# Revit family: Hydrablock P 22 30 T
name_source: partatom
category: Attrezzatura meccanica
units: mm (PartAtom-declared; Revit-internal decimal feet)

## family parameters
Basato su piano di lavoro = No
Condiviso = No
Mantieni orientamento annotazione = No
Numero OmniClass = 23.75.00.00
Punto di calcolo locali = No
Quota connettore circolare = Usa diametro
Sempre verticale = Sì
Taglio con vuoti quando caricato = No
Tipo di parte = Normale
Titolo OmniClass = Climate Control (HVAC)

## types (2) — shared parameters
Casing color = SB2014
Compressor = 1
Condensation = air
Depth = 440 mm  [stored 1.44357 ft]
Descrizione = High efficiency air cooled
Drain piping = 25 mm  [stored 0.082021 ft]
Gas = R32
Height = 1558 mm  [stored 5.11155 ft]
Installation = Outdoor installation
Min cable selection (power wiring) = 4×6 mm2 + 1×6 mm2
Power supply = 380-415V 3N~50Hz
Produttore = Midea
Series = M thermal
Water piping connections = 32 mm  [stored 0.104987 ft]
Width = 1129 mm  [stored 3.70407 ft]
clearance access behind = 300 mm
clearance access front = 3000 mm  [stored 9.84252 ft]
clearance access left = 300 mm
clearance access right = 600 mm  [stored 1.9685 ft]
zero-valued in all types: Prospetto di default

## per-type parameters (varying)
| type | Air Flow | Cooling Power Input (EWT 23⁰C, LWT 18⁰C) | Cooling Power Input(EWT 12⁰C, LWT 7⁰C) | Cooling capacity (EWT 12⁰C, LWT 7⁰C) | Cooling capacity (EWT 23⁰C, LWT 18⁰C) | Heating Power Input (EWT 30⁰C, LWT 35⁰C) | Heating Power Input (EWT 40⁰C, LWT 45⁰C) | Heating capacity (EWT 30⁰C, LWT 35⁰C) | Heating capacity (EWT 40⁰C, LWT 45⁰C) | MOP (Maximum overcurrent protection) | Minimum Circuit Amps | Modello |
| Hydrablock P 22 T | 11000.00 m³/h | 5.00 kW | 7.12 kW | 21.00 kW | 23.00 kW | 5.00 kW | 6.47 kW | 22.00 kW | 22.00 kW | 21 A | 25 A | MHC-V22W/D2RN8 |
| Hydrablock P 30 T | 11300.00 m³/h | 7.75 kW | 11.57 kW | 29.50 kW | 31.00 kW | 7.70 kW | 10.34 kW | 30.10 kW | 30.00 kW | 28 A | 29 A | MHC-V30W/D2RN8 |

note: [stored X ft] marks values corroborated as IEEE doubles in the binary element streams (Revit-internal decimal feet)

## geometry (parser evidence)
native form markers: Sweep x27
no freeform markers — native parametric forms only
